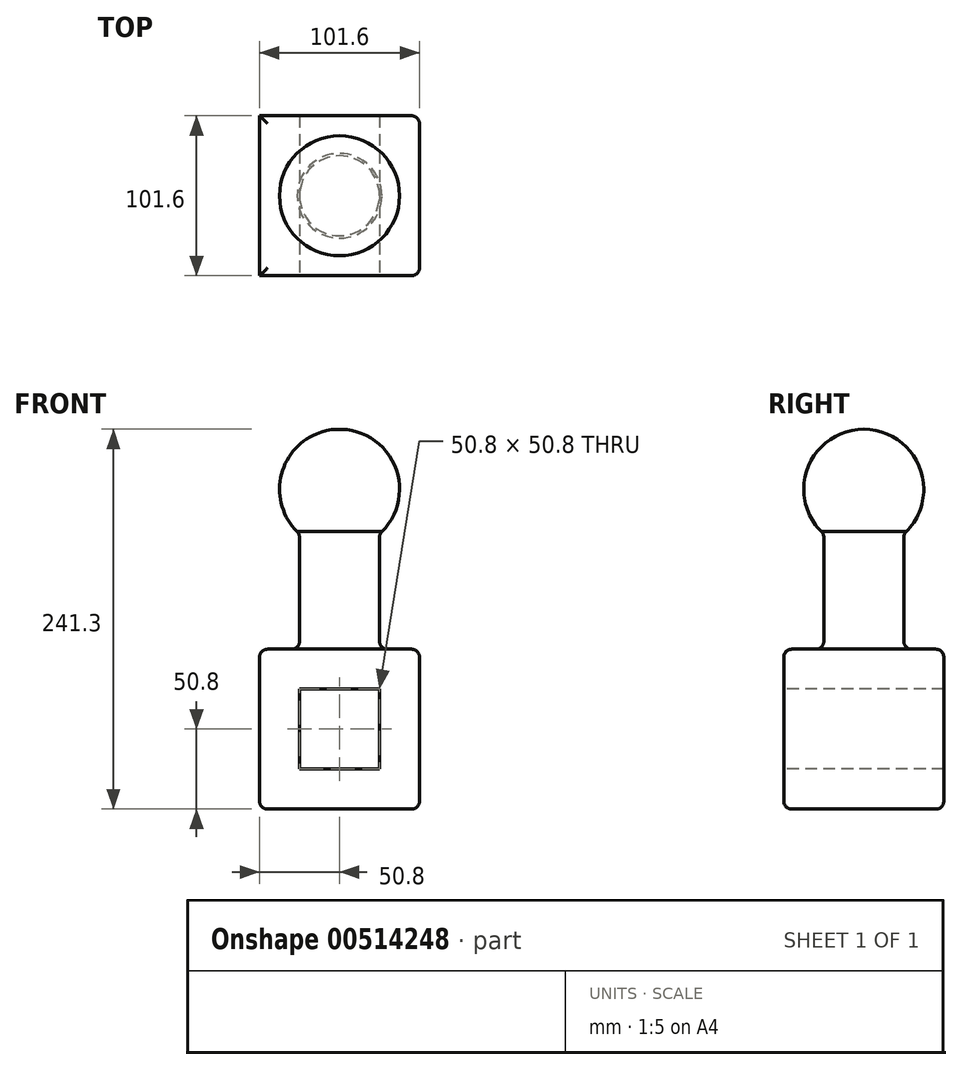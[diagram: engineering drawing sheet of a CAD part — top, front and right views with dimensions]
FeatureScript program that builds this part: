
annotation { "Feature Type Name" : "Feature", "Feature Type Description" : "" }
export const myFeature = defineFeature(function(context is Context, id is Id, definition is map)
    precondition{}
    {
        {
            var Q0;
            Q0=qCreatedBy(makeId("Top.planeOp"),FACE);
            var sketch = newSketch(context, id + "F0", { "sketchPlane" : qUnion([Q0])});
            skLineSegment(sketch, "E0.bottom", {"start": v(50.8, 50.8) * mm, "end": v(-50.8, 50.8) * mm});
            skLineSegment(sketch, "E0.top", {"start": v(50.8, -50.8) * mm, "end": v(-50.8, -50.8) * mm});
            skLineSegment(sketch, "E0.left", {"start": v(50.8, 50.8) * mm, "end": v(50.8, -50.8) * mm});
            skLineSegment(sketch, "E0.right", {"start": v(-50.8, 50.8) * mm, "end": v(-50.8, -50.8) * mm});
            skPoint(sketch, "E0.middle", {"position": v(0, 0) * mm});
            skSolve(sketch);
        }
        {
            var Q0;
            Q0=makeQuery(id+"F0.imprint","IMPRINT",FACE,{"disambiguationData":[TD([[makeQuery(id+"F0.imprint","IMPRINT",EDGE,{"derivedFrom":sQuery(id+"F0.wireOp",EDGE,"E0.bottom")}),1.0]])]});
            extrude(context, id + "F1", {"entities" : qUnion([Q0]), "depth" : 101.6 * mm});
        }
        {
            var Q0;
            Q0=makeQuery(id+"F1.opExtrude","CAP_FACE",FACE,{"disambiguationData":[OSD([sQuery(id+"F0.wireOp",EDGE,"E0.bottom"),sQuery(id+"F0.wireOp",EDGE,"E0.top"),sQuery(id+"F0.wireOp",EDGE,"E0.left"),sQuery(id+"F0.wireOp",EDGE,"E0.right")])],"isStart":false});
            var sketch = newSketch(context, id + "F2", { "sketchPlane" : qUnion([Q0])});
            skCircle(sketch, "E1", {"center": v(0, 0) * mm, "radius": 25.4 * mm});
            skSolve(sketch);
        }
        {
            var Q0;
            Q0=makeQuery(id+"F2.imprint","IMPRINT",FACE,{"disambiguationData":[TD([[makeQuery(id+"F2.imprint","IMPRINT",EDGE,{"derivedFrom":sQuery(id+"F2.wireOp",EDGE,"E1")}),1.0]])]});
            extrude(context, id + "F3", {"entities" : qUnion([Q0]), "operationType" : NewBodyOperationType.ADD, "depth" : 101.6 * mm, "offsetDistance" : 25.4 * mm});
        }
        {
            var Q0;
            Q0=makeQuery(id+"F3.opExtrude","CAP_FACE",FACE,{"disambiguationData":[OSD([sQuery(id+"F2.wireOp",EDGE,"E1")])],"isStart":false});
            var sketch = newSketch(context, id + "F4", { "sketchPlane" : qUnion([Q0])});
            skArc(sketch, "E2", {"start": v(0, -38.1) * mm, "mid": v(38.1, 0) * mm, "end": v(0, 38.1) * mm});
            skLineSegment(sketch, "E3", {"start": v(0, 38.1) * mm, "end": v(0, -38.1) * mm});
            skSolve(sketch);
        }
        {
            var Q0;
            {var subQ0=sQuery(id+"F4.wireOp",EDGE,"E2");Q0=makeQuery(id+"F4.imprint","IMPRINT",FACE,{"disambiguationData":[TD([[makeQuery(id+"F4.imprint","IMPRINT",EDGE,{"derivedFrom":subQ0}),1.0]])]});}
            var Q1;
            {var subQ0=sQuery(id+"F4.wireOp",EDGE,"E3");var subQ1=makeQuery(id+"F3.opExtrude","CAP_EDGE",EDGE,{"disambiguationData":[OSD([sQuery(id+"F2.wireOp",EDGE,"E1")])],"isStart":false});var subQ2=makeQuery(id+"F4.imprint","INTERSECT",VERTEX,{"disambiguationData":[OD(0.0)],"derivedFrom":[subQ1,subQ0]});Q1=makeQuery(id+"F4.imprint","IMPRINT",FACE,{"disambiguationData":[TD([[makeQuery(id+"F4.imprint","IMPRINT",EDGE,{"disambiguationData":[TD([[subQ2,-1.0]])],"derivedFrom":subQ0}),1.0]])]});}
            var Q2;
            Q2=sQuery(id+"F4.wireOp",EDGE,"E3");
            revolve(context, id + "F5", {"operationType" : NewBodyOperationType.ADD, "entities" : qUnion([Q0, Q1]), "axis" : qUnion([Q2]), "revolveType" : RevolveType.FULL});
        }
        {
            var Q0;
            Q0=makeQuery(id+"F1.opExtrude","SWEPT_FACE",FACE,{"disambiguationData":[OSD([sQuery(id+"F0.wireOp",EDGE,"E0.top")])]});
            var sketch = newSketch(context, id + "F6", { "sketchPlane" : qUnion([Q0])});
            skLineSegment(sketch, "E4.bottom", {"start": v(25.4, 76.2) * mm, "end": v(-25.4, 76.2) * mm});
            skLineSegment(sketch, "E4.top", {"start": v(25.4, 25.4) * mm, "end": v(-25.4, 25.4) * mm});
            skLineSegment(sketch, "E4.left", {"start": v(25.4, 76.2) * mm, "end": v(25.4, 25.4) * mm});
            skLineSegment(sketch, "E4.right", {"start": v(-25.4, 76.2) * mm, "end": v(-25.4, 25.4) * mm});
            skPoint(sketch, "E4.middle", {"position": v(0, 50.8) * mm});
            skPoint(sketch, "E4.middle.positionSnap0", {"position": v(50.8, 50.8) * mm});
            skPoint(sketch, "E4.middle.positionSnap1", {"position": v(0, 101.6) * mm});
            skPoint(sketch, "E4.centerSnap0", {"position": v(50.8, 50.8) * mm});
            skPoint(sketch, "E4.centerSnap1", {"position": v(0, 101.6) * mm});
            skSolve(sketch);
        }
        {
            var Q0;
            Q0=makeQuery(id+"F6.imprint","IMPRINT",FACE,{"disambiguationData":[TD([[makeQuery(id+"F6.imprint","IMPRINT",EDGE,{"derivedFrom":sQuery(id+"F6.wireOp",EDGE,"E4.bottom")}),1.0]])]});
            extrude(context, id + "F7", {"entities" : qUnion([Q0]), "operationType" : NewBodyOperationType.REMOVE, "oppositeDirection" : true, "depth" : 101.6 * mm, "offsetDistance" : 25.4 * mm});
        }
        {
            var Q0;
            Q0=makeQuery(id+"F3.opExtrude","SWEPT_FACE",FACE,{"disambiguationData":[OSD([sQuery(id+"F2.wireOp",EDGE,"E1")])]});
            var Q1;
            Q1=makeQuery(id+"F1.opExtrude","CAP_FACE",FACE,{"disambiguationData":[OSD([sQuery(id+"F0.wireOp",EDGE,"E0.bottom"),sQuery(id+"F0.wireOp",EDGE,"E0.top"),sQuery(id+"F0.wireOp",EDGE,"E0.left"),sQuery(id+"F0.wireOp",EDGE,"E0.right")])],"isStart":false});
            var Q2;
            Q2=makeQuery(id+"F1.opExtrude","SWEPT_FACE",FACE,{"disambiguationData":[OSD([sQuery(id+"F0.wireOp",EDGE,"E0.left")])]});
            var Q3;
            Q3=makeQuery(id+"F1.opExtrude","CAP_FACE",FACE,{"disambiguationData":[OSD([sQuery(id+"F0.wireOp",EDGE,"E0.bottom"),sQuery(id+"F0.wireOp",EDGE,"E0.top"),sQuery(id+"F0.wireOp",EDGE,"E0.left"),sQuery(id+"F0.wireOp",EDGE,"E0.right")])],"isStart":true});
            fillet(context, id + "F8", {"entities" : qUnion([Q0, Q1, Q2, Q3]), "radius" : 5.08 * mm, "tangentPropagation" : true, "allowEdgeOverflow" : false});
        }
    });
